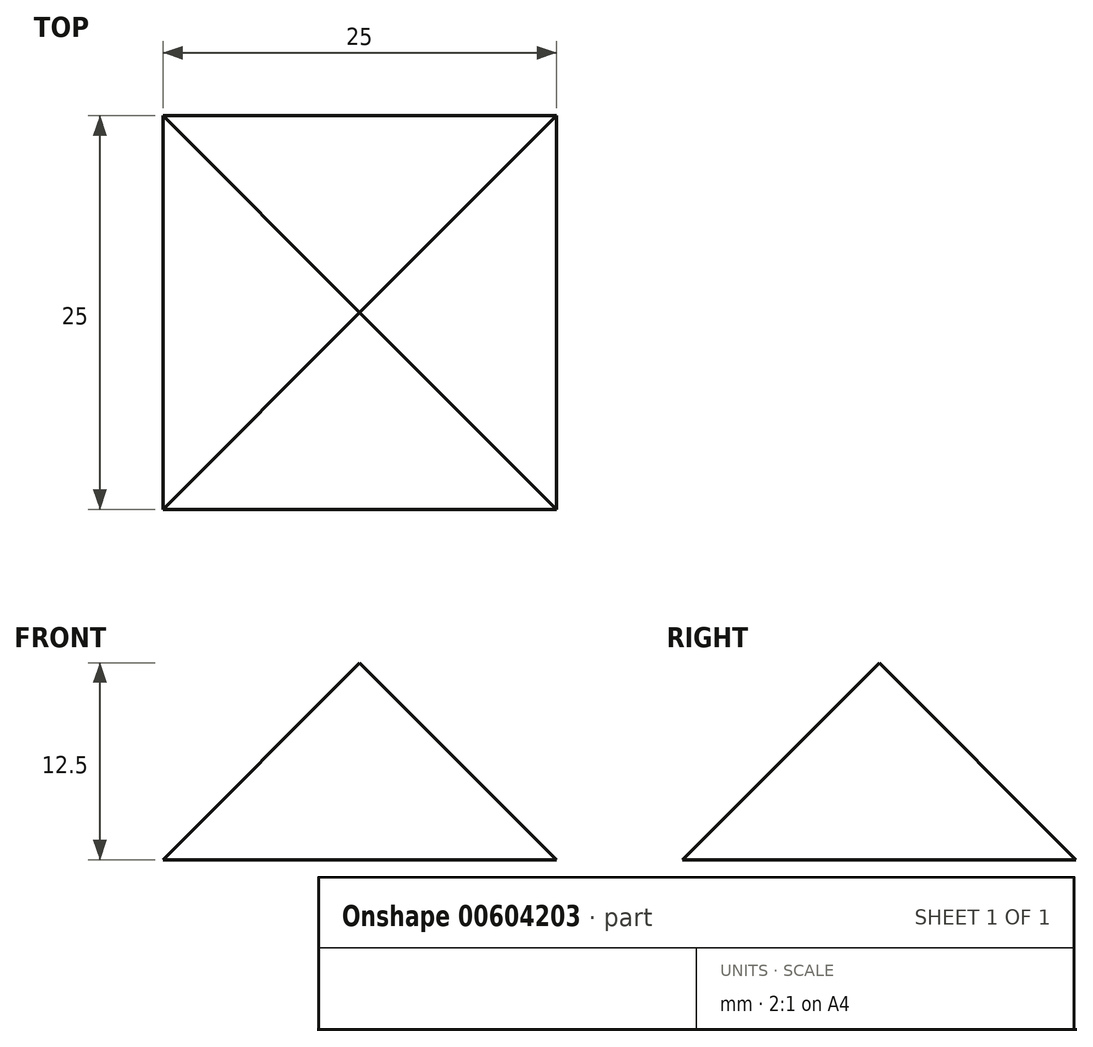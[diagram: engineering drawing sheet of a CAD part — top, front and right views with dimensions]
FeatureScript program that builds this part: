
annotation { "Feature Type Name" : "Feature", "Feature Type Description" : "" }
export const myFeature = defineFeature(function(context is Context, id is Id, definition is map)
    precondition{}
    {
        {
            var Q0;
            Q0=qCreatedBy(makeId("Top.planeOp"),FACE);
            var sketch = newSketch(context, id + "F0", { "sketchPlane" : qUnion([Q0])});
            skLineSegment(sketch, "E0.bottom", {"start": v(-12.5, 12.5) * mm, "end": v(12.5, 12.5) * mm});
            skLineSegment(sketch, "E0.top", {"start": v(-12.5, -12.5) * mm, "end": v(12.5, -12.5) * mm});
            skLineSegment(sketch, "E0.left", {"start": v(-12.5, 12.5) * mm, "end": v(-12.5, -12.5) * mm});
            skLineSegment(sketch, "E0.right", {"start": v(12.5, 12.5) * mm, "end": v(12.5, -12.5) * mm});
            skSolve(sketch);
        }
        {
            var Q0;
            Q0=qSketchRegion(id+"F0",true);
            extrude(context, id + "F1", {"entities" : qUnion([Q0]), "depth" : 25 * mm, "offsetDistance" : 25 * mm});
        }
        {
            var Q0;
            Q0=qCreatedBy(makeId("Right.planeOp"),FACE);
            var sketch = newSketch(context, id + "F2", { "sketchPlane" : qUnion([Q0])});
            skLineSegment(sketch, "E1.0.1", {"start": v(12.5, 0) * mm, "end": v(12.5, 25) * mm});
            skLineSegment(sketch, "E1.0.2", {"start": v(12.5, 25) * mm, "end": v(-12.5, 25) * mm});
            skLineSegment(sketch, "E1.0.3", {"start": v(-12.5, 25) * mm, "end": v(-12.5, 0) * mm});
            skLineSegment(sketch, "E2", {"start": v(-12.5, 0) * mm, "end": v(0, 12.5) * mm});
            skLineSegment(sketch, "E3", {"start": v(12.5, 0) * mm, "end": v(0, 12.5) * mm});
            skSolve(sketch);
        }
        {
            var Q0;
            Q0 = qSketchRegion(id + "F2", true);
            extrude(context, id + "F3", {"entities" : qUnion([Q0]), "operationType" : NewBodyOperationType.REMOVE, "endBound" : BoundingType.THROUGH_ALL, "oppositeDirection" : true, "depth" : 25 * mm, "offsetDistance" : 25 * mm, "hasSecondDirection" : true, "secondDirectionBound" : SecondDirectionBoundingType.THROUGH_ALL, "secondDirectionOppositeDirection" : false, "secondDirectionDepth" : 25 * mm});
        }
        {
            var Q0;
            Q0=qCreatedBy(makeId("Front.planeOp"),FACE);
            var sketch = newSketch(context, id + "F4", { "sketchPlane" : qUnion([Q0])});
            skLineSegment(sketch, "E4.0.1", {"start": v(12.5, 0) * mm, "end": v(12.5, 25) * mm});
            skLineSegment(sketch, "E4.0.2", {"start": v(12.5, 25) * mm, "end": v(-12.5, 25) * mm});
            skLineSegment(sketch, "E4.0.3", {"start": v(-12.5, 25) * mm, "end": v(-12.5, 0) * mm});
            skLineSegment(sketch, "E5", {"start": v(-12.5, 0) * mm, "end": v(0, 12.5) * mm});
            skLineSegment(sketch, "E6", {"start": v(12.5, 0) * mm, "end": v(0, 12.5) * mm});
            skSolve(sketch);
        }
        {
            var Q0;
            Q0 = qSketchRegion(id + "F4", true);
            extrude(context, id + "F5", {"entities" : qUnion([Q0]), "operationType" : NewBodyOperationType.REMOVE, "endBound" : BoundingType.THROUGH_ALL, "oppositeDirection" : true, "depth" : 25 * mm, "offsetDistance" : 25 * mm, "hasSecondDirection" : true, "secondDirectionBound" : SecondDirectionBoundingType.THROUGH_ALL, "secondDirectionOppositeDirection" : false, "secondDirectionDepth" : 25 * mm});
        }
    });
